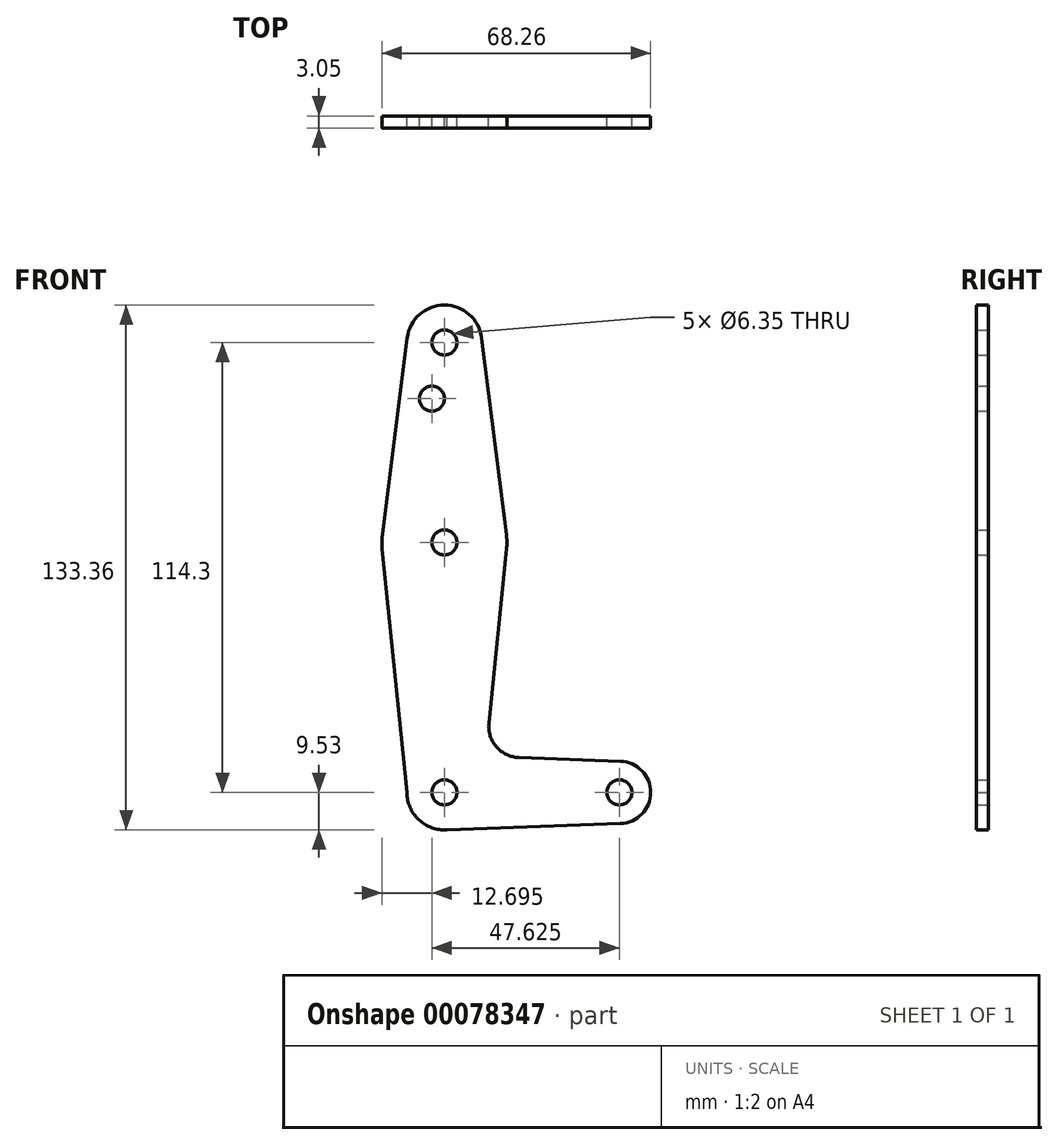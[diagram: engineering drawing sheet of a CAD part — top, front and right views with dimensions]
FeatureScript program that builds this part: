
annotation { "Feature Type Name" : "Feature", "Feature Type Description" : "" }
export const myFeature = defineFeature(function(context is Context, id is Id, definition is map)
    precondition{}
    {
        {
            var Q0;
            Q0=qCreatedBy(makeId("Front.planeOp"),FACE);
            var sketch = newSketch(context, id + "F0", { "sketchPlane" : qUnion([Q0])});
            skLineSegment(sketch, "E0", {"start": v(0, 0) * mm, "end": v(44.45, 0) * mm, "construction": true});
            skLineSegment(sketch, "E1", {"start": v(0, 0) * mm, "end": v(0, 114.3) * mm, "construction": true});
            skCircle(sketch, "E2", {"center": v(0, 114.3) * mm, "radius": 9.53 * mm});
            skCircle(sketch, "E3", {"center": v(0, 0) * mm, "radius": 9.53 * mm});
            skCircle(sketch, "E4", {"center": v(0, 63.5) * mm, "radius": 15.88 * mm});
            skCircle(sketch, "E5", {"center": v(44.45, 0) * mm, "radius": 7.94 * mm});
            skLineSegment(sketch, "E6", {"start": v(-9.45, 115.5) * mm, "end": v(-15.75, 65.48) * mm});
            skLineSegment(sketch, "E7", {"start": v(-9.52, 0) * mm, "end": v(-15.8, 61.9) * mm});
            skLineSegment(sketch, "E8", {"start": v(11.3, 17.6) * mm, "end": v(15.8, 61.9) * mm});
            skLineSegment(sketch, "E9", {"start": v(9.45, 115.5) * mm, "end": v(15.75, 65.48) * mm});
            skLineSegment(sketch, "E10", {"start": v(18.93, 8.85) * mm, "end": v(44.73, 7.93) * mm});
            skLineSegment(sketch, "E11", {"start": v(0, -9.52) * mm, "end": v(44.73, -7.93) * mm});
            skCircle(sketch, "E12", {"center": v(0, 114.3) * mm, "radius": 3.18 * mm});
            skCircle(sketch, "E13", {"center": v(-3.18, 100.03) * mm, "radius": 3.18 * mm});
            skCircle(sketch, "E14", {"center": v(0, 63.5) * mm, "radius": 3.18 * mm});
            skCircle(sketch, "E15", {"center": v(0, 0) * mm, "radius": 3.18 * mm});
            skCircle(sketch, "E16", {"center": v(44.45, 0) * mm, "radius": 3.18 * mm});
            skArc(sketch, "E17.filletArc", {"start": v(11.3, 17.6) * mm, "mid": v(13.22, 11.57) * mm, "end": v(18.93, 8.85) * mm});
            skSolve(sketch);
        }
        {
            var Q0;
            Q0 = qSketchRegion(id + "F0", true);
            extrude(context, id + "F1", {"entities" : qUnion([Q0]), "depth" : 3.05 * mm});
        }
    });
